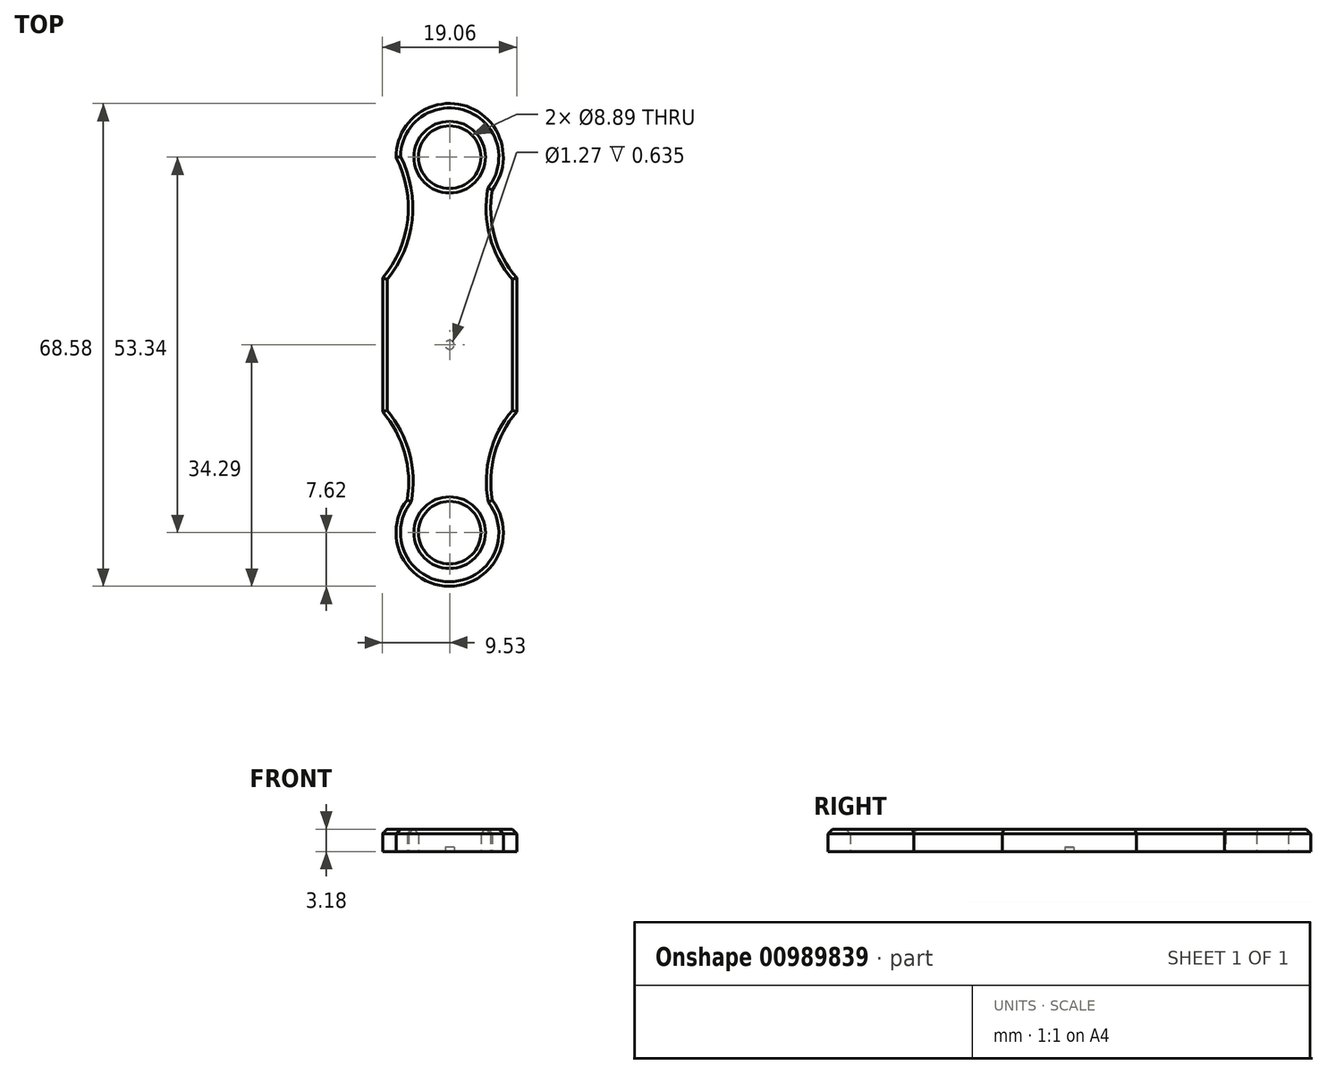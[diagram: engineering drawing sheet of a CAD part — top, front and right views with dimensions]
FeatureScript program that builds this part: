
annotation { "Feature Type Name" : "Feature", "Feature Type Description" : "" }
export const myFeature = defineFeature(function(context is Context, id is Id, definition is map)
    precondition{}
    {
        {
            var Q0;
            Q0=qCreatedBy(makeId("Top.planeOp"),FACE);
            var sketch = newSketch(context, id + "F0", { "sketchPlane" : qUnion([Q0])});
            skLineSegment(sketch, "E0.bottom", {"start": v(-9.52, 9.53) * mm, "end": v(9.53, 9.53) * mm});
            skLineSegment(sketch, "E0.top", {"start": v(-9.53, -9.53) * mm, "end": v(9.53, -9.53) * mm});
            skLineSegment(sketch, "E0.left", {"start": v(-9.52, 9.53) * mm, "end": v(-9.53, -9.53) * mm});
            skLineSegment(sketch, "E0.right", {"start": v(9.53, 9.53) * mm, "end": v(9.53, -9.53) * mm});
            skPoint(sketch, "E0.middle", {"position": v(0, 0) * mm});
            skCircle(sketch, "E1", {"center": v(0, -26.67) * mm, "radius": 7.62 * mm});
            skLineSegment(sketch, "E2", {"start": v(0, -26.67) * mm, "end": v(0, 0) * mm, "construction": true});
            skLineSegment(sketch, "E3", {"start": v(-7.62, -26.67) * mm, "end": v(-9.52, -9.52) * mm, "construction": true});
            skLineSegment(sketch, "E4", {"start": v(9.52, -9.53) * mm, "end": v(7.66, -26.67) * mm, "construction": true});
            skLineSegment(sketch, "E5", {"start": v(0, -9.53) * mm, "end": v(0, -19.05) * mm, "construction": true});
            skLineSegment(sketch, "E6", {"start": v(0, -19.05) * mm, "end": v(0, -13.97) * mm, "construction": true});
            skArc(sketch, "E7", {"start": v(-7.62, -26.67) * mm, "mid": v(-5.91, -17.8) * mm, "end": v(-9.52, -9.52) * mm});
            skArc(sketch, "E8", {"start": v(9.52, -9.53) * mm, "mid": v(5.94, -17.8) * mm, "end": v(7.66, -26.67) * mm});
            skCircle(sketch, "E9", {"center": v(0, -26.67) * mm, "radius": 4.45 * mm});
            skLineSegment(sketch, "E10", {"start": v(0, 0) * mm, "end": v(0, 26.67) * mm, "construction": true});
            skCircle(sketch, "E11", {"center": v(0, 26.67) * mm, "radius": 7.62 * mm});
            skCircle(sketch, "E12", {"center": v(0, 26.67) * mm, "radius": 4.45 * mm});
            skLineSegment(sketch, "E13", {"start": v(-9.52, 9.52) * mm, "end": v(-7.66, 26.67) * mm, "construction": true});
            skLineSegment(sketch, "E14", {"start": v(-7.66, 26.67) * mm, "end": v(7.62, 26.67) * mm, "construction": true});
            skLineSegment(sketch, "E15", {"start": v(7.62, 26.67) * mm, "end": v(9.53, 9.53) * mm, "construction": true});
            skArc(sketch, "E16", {"start": v(-9.52, 9.53) * mm, "mid": v(-5.94, 17.8) * mm, "end": v(-7.66, 26.67) * mm});
            skArc(sketch, "E17", {"start": v(7.62, 26.67) * mm, "mid": v(5.91, 17.8) * mm, "end": v(9.52, 9.52) * mm});
            skCircle(sketch, "E18", {"center": v(0, 0) * mm, "radius": 0.64 * mm});
            skSolve(sketch);
        }
        {
            var Q0;
            Q0=makeQuery(id+"F0.imprint","IMPRINT",FACE,{"disambiguationData":[TD([[makeQuery(id+"F0.imprint","IMPRINT",EDGE,{"derivedFrom":sQuery(id+"F0.wireOp",EDGE,"E0.bottom")}),-1.0]])]});
            var Q1;
            {var subQ0=sQuery(id+"F0.wireOp",EDGE,"E0.top");Q1=makeQuery(id+"F0.imprint","IMPRINT",FACE,{"disambiguationData":[TD([[makeQuery(id+"F0.imprint","IMPRINT",EDGE,{"derivedFrom":subQ0}),-1.0]])]});}
            var Q2;
            {var subQ0=sQuery(id+"F0.wireOp",EDGE,"E8");var subQ1=sQuery(id+"F0.wireOp",EDGE,"E1");var subQ2=makeQuery(id+"F0.imprint","INTERSECT",VERTEX,{"disambiguationData":[OD(1.0)],"derivedFrom":[subQ1,subQ0]});Q2=makeQuery(id+"F0.imprint","IMPRINT",FACE,{"disambiguationData":[TD([[makeQuery(id+"F0.imprint","IMPRINT",EDGE,{"disambiguationData":[TD([[subQ2,-1.0]])],"derivedFrom":subQ1}),1.0]])]});}
            var Q3;
            {var subQ0=sQuery(id+"F0.wireOp",EDGE,"E7");var subQ1=sQuery(id+"F0.wireOp",EDGE,"E1");var subQ2=makeQuery(id+"F0.imprint","INTERSECT",VERTEX,{"disambiguationData":[OD(0.0)],"derivedFrom":[subQ1,subQ0]});Q3=makeQuery(id+"F0.imprint","IMPRINT",FACE,{"disambiguationData":[TD([[makeQuery(id+"F0.imprint","IMPRINT",EDGE,{"disambiguationData":[TD([[subQ2,1.0]])],"derivedFrom":subQ1}),1.0]])]});}
            var Q4;
            {var subQ0=sQuery(id+"F0.wireOp",EDGE,"E8");var subQ1=sQuery(id+"F0.wireOp",EDGE,"E1");var subQ2=makeQuery(id+"F0.imprint","INTERSECT",VERTEX,{"disambiguationData":[OD(0.0)],"derivedFrom":[subQ1,subQ0]});Q4=makeQuery(id+"F0.imprint","IMPRINT",FACE,{"disambiguationData":[TD([[makeQuery(id+"F0.imprint","IMPRINT",EDGE,{"disambiguationData":[TD([[subQ2,-1.0]])],"derivedFrom":subQ1}),1.0]])]});}
            var Q5;
            {var subQ0=sQuery(id+"F0.wireOp",EDGE,"E0.bottom");Q5=makeQuery(id+"F0.imprint","IMPRINT",FACE,{"disambiguationData":[TD([[makeQuery(id+"F0.imprint","IMPRINT",EDGE,{"derivedFrom":subQ0}),1.0]])]});}
            var Q6;
            Q6=makeQuery(id+"F0.imprint","IMPRINT",FACE,{"disambiguationData":[TD([[makeQuery(id+"F0.imprint","IMPRINT",EDGE,{"derivedFrom":sQuery(id+"F0.wireOp",EDGE,"E12")}),-1.0]])]});
            var Q7;
            {var subQ0=sQuery(id+"F0.wireOp",EDGE,"E16");var subQ1=sQuery(id+"F0.wireOp",EDGE,"E11");var subQ2=makeQuery(id+"F0.imprint","INTERSECT",VERTEX,{"disambiguationData":[OD(0.0)],"derivedFrom":[subQ1,subQ0]});Q7=makeQuery(id+"F0.imprint","IMPRINT",FACE,{"disambiguationData":[TD([[makeQuery(id+"F0.imprint","IMPRINT",EDGE,{"disambiguationData":[TD([[subQ2,-1.0]])],"derivedFrom":subQ1}),1.0]])]});}
            var Q8;
            {var subQ0=sQuery(id+"F0.wireOp",EDGE,"E17");var subQ1=sQuery(id+"F0.wireOp",EDGE,"E11");var subQ2=makeQuery(id+"F0.imprint","INTERSECT",VERTEX,{"disambiguationData":[OD(0.0)],"derivedFrom":[subQ1,subQ0]});Q8=makeQuery(id+"F0.imprint","IMPRINT",FACE,{"disambiguationData":[TD([[makeQuery(id+"F0.imprint","IMPRINT",EDGE,{"disambiguationData":[TD([[subQ2,1.0]])],"derivedFrom":subQ1}),1.0]])]});}
            var Q9;
            Q9=makeQuery(id+"F0.imprint","IMPRINT",FACE,{"disambiguationData":[TD([[makeQuery(id+"F0.imprint","IMPRINT",EDGE,{"derivedFrom":sQuery(id+"F0.wireOp",EDGE,"E18")}),1.0]])]});
            extrude(context, id + "F1", {"entities" : qUnion([Q0, Q1, Q2, Q3, Q4, Q5, Q6, Q7, Q8, Q9]), "depth" : 3.17 * mm, "offsetDistance" : 25.4 * mm});
        }
        {
            var Q0;
            Q0=makeQuery(id+"F1.opExtrude","CAP_FACE",FACE,{"disambiguationData":[OSD([sQuery(id+"F0.wireOp",EDGE,"E0.bottom"),sQuery(id+"F0.wireOp",EDGE,"E0.left"),sQuery(id+"F0.wireOp",EDGE,"E0.right"),sQuery(id+"F0.wireOp",EDGE,"E1"),sQuery(id+"F0.wireOp",EDGE,"E7"),sQuery(id+"F0.wireOp",EDGE,"E8"),sQuery(id+"F0.wireOp",EDGE,"E9")])],"isStart":false});
            chamfer(context, id + "F2", {"entities" : qUnion([Q0]), "width" : 0.64 * mm, "tangentPropagation" : true});
        }
        {
            var Q0;
            Q0=makeQuery(id+"F0.imprint","IMPRINT",FACE,{"disambiguationData":[TD([[makeQuery(id+"F0.imprint","IMPRINT",EDGE,{"derivedFrom":sQuery(id+"F0.wireOp",EDGE,"E18")}),1.0]])]});
            extrude(context, id + "F3", {"entities" : qUnion([Q0]), "operationType" : NewBodyOperationType.REMOVE, "depth" : 0.64 * mm, "offsetDistance" : 25.4 * mm});
        }
    });
